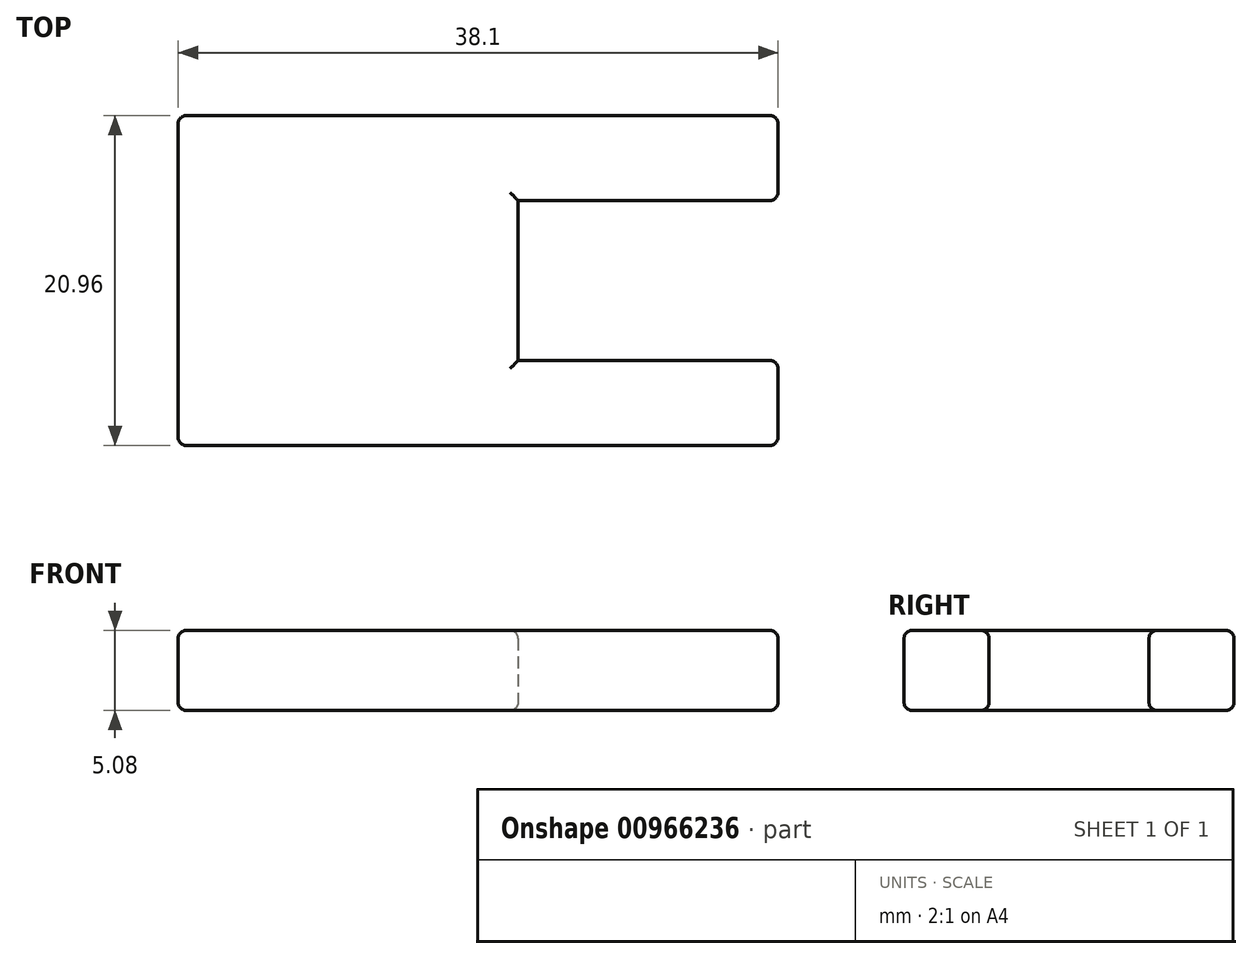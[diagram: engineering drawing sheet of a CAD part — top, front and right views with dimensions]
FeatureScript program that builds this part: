
annotation { "Feature Type Name" : "Feature", "Feature Type Description" : "" }
export const myFeature = defineFeature(function(context is Context, id is Id, definition is map)
    precondition{}
    {
        {
            var Q0;
            Q0=qCreatedBy(makeId("Top.planeOp"),FACE);
            var sketch = newSketch(context, id + "F0", { "sketchPlane" : qUnion([Q0])});
            skLineSegment(sketch, "E0.bottom", {"start": v(-19.05, 10.48) * mm, "end": v(19.05, 10.48) * mm});
            skLineSegment(sketch, "E0.top", {"start": v(-19.05, -10.48) * mm, "end": v(19.05, -10.48) * mm});
            skLineSegment(sketch, "E0.left", {"start": v(-19.05, 10.48) * mm, "end": v(-19.05, -10.48) * mm});
            skLineSegment(sketch, "E0.right", {"start": v(19.05, 10.48) * mm, "end": v(19.05, 5.08) * mm});
            skPoint(sketch, "E0.middle", {"position": v(0, 0) * mm});
            skLineSegment(sketch, "E1.bottom", {"start": v(19.05, 5.08) * mm, "end": v(2.54, 5.08) * mm});
            skLineSegment(sketch, "E1.top", {"start": v(19.05, -5.08) * mm, "end": v(2.54, -5.08) * mm});
            skLineSegment(sketch, "E1.right", {"start": v(2.54, 5.08) * mm, "end": v(2.54, -5.08) * mm});
            skPoint(sketch, "E2", {"position": v(19.05, 5.08) * mm});
            skPoint(sketch, "E3", {"position": v(19.05, -5.08) * mm});
            skLineSegment(sketch, "E4.trimOffspring", {"start": v(19.05, -5.08) * mm, "end": v(19.05, -10.48) * mm});
            skSolve(sketch);
        }
        {
            var Q0;
            Q0=makeQuery(id+"F0.imprint","IMPRINT",FACE,{"disambiguationData":[TD([[makeQuery(id+"F0.imprint","IMPRINT",EDGE,{"derivedFrom":sQuery(id+"F0.wireOp",EDGE,"E0.bottom")}),-1.0]])]});
            extrude(context, id + "F1", {"entities" : qUnion([Q0]), "depth" : 5.08 * mm});
        }
        {
            var Q0;
            Q0=makeQuery(id+"F1.opExtrude","CAP_EDGE",EDGE,{"disambiguationData":[OSD([sQuery(id+"F0.wireOp",EDGE,"E1.right")])],"isStart":false});
            var Q1;
            Q1=makeQuery(id+"F1.opExtrude","CAP_EDGE",EDGE,{"disambiguationData":[OSD([sQuery(id+"F0.wireOp",EDGE,"E1.right")])],"isStart":true});
            var Q2;
            Q2=makeQuery(id+"F1.opExtrude","CAP_EDGE",EDGE,{"disambiguationData":[OSD([sQuery(id+"F0.wireOp",EDGE,"E1.bottom")])],"isStart":true});
            var Q3;
            Q3=makeQuery(id+"F1.opExtrude","CAP_EDGE",EDGE,{"disambiguationData":[OSD([sQuery(id+"F0.wireOp",EDGE,"E1.bottom")])],"isStart":false});
            var Q4;
            Q4=makeQuery(id+"F1.opExtrude","CAP_EDGE",EDGE,{"disambiguationData":[OSD([sQuery(id+"F0.wireOp",EDGE,"E1.top")])],"isStart":false});
            var Q5;
            Q5=makeQuery(id+"F1.opExtrude","CAP_EDGE",EDGE,{"disambiguationData":[OSD([sQuery(id+"F0.wireOp",EDGE,"E1.top")])],"isStart":true});
            var Q6;
            Q6=makeQuery(id+"F1.opExtrude","SWEPT_EDGE",EDGE,{"disambiguationData":[OSD([sQuery(id+"F0.wireOp",EDGE,"E0.top"),sQuery(id+"F0.wireOp",EDGE,"E4.trimOffspring")])]});
            var Q7;
            Q7=makeQuery(id+"F1.opExtrude","CAP_EDGE",EDGE,{"disambiguationData":[OSD([sQuery(id+"F0.wireOp",EDGE,"E0.top")])],"isStart":false});
            var Q8;
            Q8=makeQuery(id+"F1.opExtrude","CAP_EDGE",EDGE,{"disambiguationData":[OSD([sQuery(id+"F0.wireOp",EDGE,"E0.top")])],"isStart":true});
            var Q9;
            Q9=makeQuery(id+"F1.opExtrude","SWEPT_EDGE",EDGE,{"disambiguationData":[OSD([sQuery(id+"F0.wireOp",EDGE,"E0.top"),sQuery(id+"F0.wireOp",EDGE,"E0.left")])]});
            var Q10;
            Q10=makeQuery(id+"F1.opExtrude","SWEPT_EDGE",EDGE,{"disambiguationData":[OSD([sQuery(id+"F0.wireOp",EDGE,"E0.right"),sQuery(id+"F0.wireOp",EDGE,"E1.bottom")])]});
            var Q11;
            Q11=makeQuery(id+"F1.opExtrude","SWEPT_EDGE",EDGE,{"disambiguationData":[OSD([sQuery(id+"F0.wireOp",EDGE,"E1.top"),sQuery(id+"F0.wireOp",EDGE,"E4.trimOffspring")])]});
            var Q12;
            Q12=makeQuery(id+"F1.opExtrude","CAP_EDGE",EDGE,{"disambiguationData":[OSD([sQuery(id+"F0.wireOp",EDGE,"E0.bottom")])],"isStart":true});
            var Q13;
            Q13=makeQuery(id+"F1.opExtrude","SWEPT_EDGE",EDGE,{"disambiguationData":[OSD([sQuery(id+"F0.wireOp",EDGE,"E0.bottom"),sQuery(id+"F0.wireOp",EDGE,"E0.right")])]});
            var Q14;
            Q14=makeQuery(id+"F1.opExtrude","CAP_EDGE",EDGE,{"disambiguationData":[OSD([sQuery(id+"F0.wireOp",EDGE,"E0.bottom")])],"isStart":false});
            var Q15;
            Q15=makeQuery(id+"F1.opExtrude","SWEPT_EDGE",EDGE,{"disambiguationData":[OSD([sQuery(id+"F0.wireOp",EDGE,"E0.bottom"),sQuery(id+"F0.wireOp",EDGE,"E0.left")])]});
            var Q16;
            Q16=makeQuery(id+"F1.opExtrude","CAP_EDGE",EDGE,{"disambiguationData":[OSD([sQuery(id+"F0.wireOp",EDGE,"E0.left")])],"isStart":false});
            var Q17;
            Q17=makeQuery(id+"F1.opExtrude","CAP_EDGE",EDGE,{"disambiguationData":[OSD([sQuery(id+"F0.wireOp",EDGE,"E0.left")])],"isStart":true});
            var Q18;
            Q18=makeQuery(id+"F1.opExtrude","CAP_EDGE",EDGE,{"disambiguationData":[OSD([sQuery(id+"F0.wireOp",EDGE,"E0.right")])],"isStart":false});
            var Q19;
            Q19=makeQuery(id+"F1.opExtrude","CAP_EDGE",EDGE,{"disambiguationData":[OSD([sQuery(id+"F0.wireOp",EDGE,"E0.right")])],"isStart":true});
            var Q20;
            Q20=makeQuery(id+"F1.opExtrude","CAP_EDGE",EDGE,{"disambiguationData":[OSD([sQuery(id+"F0.wireOp",EDGE,"E4.trimOffspring")])],"isStart":true});
            var Q21;
            Q21=makeQuery(id+"F1.opExtrude","CAP_EDGE",EDGE,{"disambiguationData":[OSD([sQuery(id+"F0.wireOp",EDGE,"E4.trimOffspring")])],"isStart":false});
            fillet(context, id + "F2", {"entities" : qUnion([Q0, Q1, Q2, Q3, Q4, Q5, Q6, Q7, Q8, Q9, Q10, Q11, Q12, Q13, Q14, Q15, Q16, Q17, Q18, Q19, Q20, Q21]), "radius" : 0.5 * mm, "tangentPropagation" : true, "allowEdgeOverflow" : false});
        }
    });
